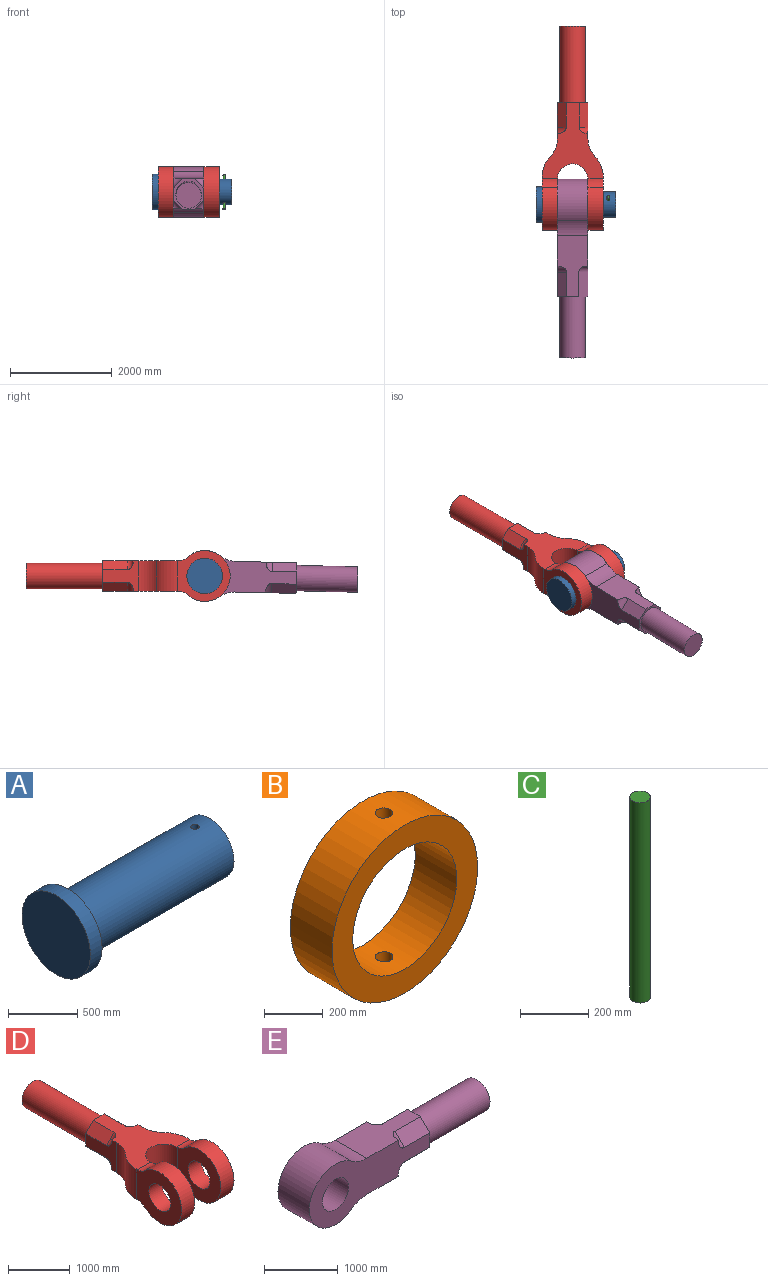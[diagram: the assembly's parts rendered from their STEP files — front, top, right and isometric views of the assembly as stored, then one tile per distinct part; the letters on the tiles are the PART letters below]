
ASSEMBLY  parts=5 mates=5
PART A: 6 faces, bbox 1570x700x700 mm
  f0: cylinder r=250mm len=1450mm, axis (-1,0,0), area 2272006.1mm2, adj f1,f2,f5
  f1: plane 500x500mm, normal (1,0,0), area 196349.5mm2, adj f0
  f2: plane 700x700mm, normal (1,0,0), area 188495.6mm2, adj f0,f3
  f3: cylinder r=350mm len=700mm, axis (-1,0,0), area 263893.8mm2, adj f2,f4
  f4: plane 700x700mm, normal (-1,0,0), area 384845.1mm2, adj f3
  f5: cylinder r=30mm len=500mm, axis (0,0,-1), area 93907.4mm2, adj f0
PART B: 6 faces, bbox 700x200x700 mm
  f0: cylinder r=250mm len=500mm, axis (0,1,0), area 308511.8mm2, adj f2,f3,f4,f5
  f1: cylinder r=350mm len=700mm, axis (0,1,0), area 434178.1mm2, adj f2,f3,f4,f5
  f2: plane 700x700mm, normal (0,-1,0), area 188495.6mm2, adj f0,f1
  f3: plane 700x700mm, normal (0,1,0), area 188495.6mm2, adj f0,f1
  f4: cylinder r=30mm len=101.81mm, axis (0,0,1), area 18898.3mm2, adj f0,f1
  f5: cylinder r=30mm len=101.81mm, axis (0,0,1), area 18898.2mm2, adj f0,f1
PART C: 3 faces, bbox 60x60x720 mm
  f0: cylinder r=30mm len=720mm, axis (0,0,-1), area 135716.8mm2, adj f1,f2
  f1: plane 60x60mm, normal (0,0,1), area 2827.4mm2, adj f0
  f2: plane 60x60mm, normal (0,0,-1), area 2827.4mm2, adj f0
PART D: 36 faces, bbox 1200x4007x1000 mm
  f0: plane 600x600mm, normal (0,1,0), area 103098.5mm2, adj f1,f2,f9,f18,f22,f24,f26,f28
  f1: plane 705.02x600mm, normal (-1,0,0), area 222950.5mm2, adj f0,f2,f7,f18,f24,f25,f26,f27
  f2: plane 1490.1x1200mm, normal (0,0,1), area 810833.6mm2, adj f0,f1,f3,f6,f7,f8,f9,f10
  f3: plane 1040x1000mm, normal (-1,0,0), area 635026.5mm2, adj f2,f6,f13,f15,f17,f18,f21
  f4: plane 1000x1000mm, normal (-1,0,0), area 611025.2mm2, adj f12,f14,f16,f19,f20
  f5: plane 1000x1000mm, normal (1,0,0), area 611025.2mm2, adj f12,f13,f15,f17,f21
  f6: cylinder r=600mm len=600mm, axis (0,0,1), area 272324.3mm2, adj f2,f3,f7,f18
  f7: cylinder r=500mm len=600mm, axis (0,0,1), area 226936.9mm2, adj f1,f2,f6,f18
  f8: cylinder r=600mm len=600mm, axis (0,0,1), area 272324.3mm2, adj f2,f10,f11,f18
  f9: plane 705.02x600mm, normal (1,0,0), area 222950.5mm2, adj f0,f2,f10,f18,f22,f23,f28,f29
  f10: cylinder r=500mm len=600mm, axis (0,0,1), area 226936.9mm2, adj f2,f8,f9,f18
  f11: plane 1040x1000mm, normal (1,0,0), area 635026.5mm2, adj f2,f8,f14,f16,f18,f19,f20
  f12: cylinder r=300mm len=600.39mm, axis (0,0,1), area 565489.3mm2, adj f2,f4,f5,f15,f16,f17,f18,f19
  f13: cylinder r=500mm len=1000mm, axis (1,0,0), area 695514.2mm2, adj f3,f5,f15,f17
  f14: cylinder r=500mm len=1000mm, axis (1,0,0), area 695514.2mm2, adj f4,f11,f16,f19
  f15: cylinder r=250mm len=300.16mm, axis (1,0,0), area 56069.4mm2, adj f2,f3,f5,f12,f13
  f16: cylinder r=250mm len=300.16mm, axis (1,0,0), area 56069.4mm2, adj f2,f4,f11,f12,f14
  f17: cylinder r=250mm len=300.16mm, axis (1,0,0), area 56069.4mm2, adj f3,f5,f12,f13,f18
  f18: plane 1490.1x1200mm, normal (0,0,-1), area 810833.6mm2, adj f0,f1,f3,f6,f7,f8,f9,f10
  f19: cylinder r=250mm len=300.16mm, axis (1,0,0), area 56069.4mm2, adj f4,f11,f12,f14,f18
  f20: cylinder r=250mm len=500mm, axis (1,0,0), area 471238.9mm2, adj f4,f11
  f21: cylinder r=250mm len=500mm, axis (1,0,0), area 471238.9mm2, adj f3,f5
  f22: plane 480x174mm, normal (0.71,0,-0.71), area 118115.1mm2, adj f0,f9,f18,f33
  f23: plane 4.29x4.29mm, normal (0,1,0), area 9.2mm2, adj f9,f18,f33
  f24: plane 480x174mm, normal (-0.71,0,-0.71), area 118115.1mm2, adj f0,f1,f18,f32
  f25: plane 4.29x4.29mm, normal (0,1,0), area 9.2mm2, adj f1,f18,f32
  f26: plane 480x174mm, normal (-0.71,0,0.71), area 118115.1mm2, adj f0,f1,f2,f35
  f27: plane 4.29x4.29mm, normal (0,1,0), area 9.2mm2, adj f1,f2,f35
  f28: plane 480x174mm, normal (0.71,0,0.71), area 118115.1mm2, adj f0,f2,f9,f34
  f29: plane 4.29x4.29mm, normal (0,1,0), area 9.2mm2, adj f2,f9,f34
  f30: cylinder r=250mm len=1507mm, axis (0,-1,0), area 2367190.1mm2, adj f0,f31
  f31: plane 500x500mm, normal (0,1,0), area 196349.5mm2, adj f30
  f32: cylinder r=120mm len=258.85mm, axis (0.71,0,-0.71), area 29944.8mm2, adj f1,f18,f24,f25
  f33: cylinder r=120mm len=258.85mm, axis (0.71,0,0.71), area 29944.8mm2, adj f9,f18,f22,f23
  f34: cylinder r=120mm len=258.85mm, axis (-0.71,0,0.71), area 29944.8mm2, adj f2,f9,f28,f29
  f35: cylinder r=120mm len=258.85mm, axis (-0.71,0,-0.71), area 29944.8mm2, adj f1,f2,f26,f27
PART E: 23 faces, bbox 3505x769.7x1000 mm
  f0: plane 1200x600mm, normal (0,0,1), area 512020.6mm2, adj f2,f3,f6,f8,f9,f10,f13,f14
  f1: plane 1200x600mm, normal (0,0,-1), area 512020.6mm2, adj f2,f5,f6,f8,f11,f12,f15,f16
  f2: plane 2300x1000mm, normal (0,-1,0), area 1188370.1mm2, adj f0,f1,f3,f4,f5,f6,f7,f13
  f3: cylinder r=500mm len=600mm, axis (0,1,0), area 193050.3mm2, adj f0,f2,f4,f8
  f4: cylinder r=500mm len=1000mm, axis (0,1,0), area 1328578.5mm2, adj f2,f3,f5,f8
  f5: cylinder r=500mm len=600mm, axis (0,1,0), area 193050.3mm2, adj f1,f2,f4,f8
  f6: plane 600x600mm, normal (1,0,0), area 98417.7mm2, adj f0,f1,f2,f8,f9,f11,f13,f15
  f7: cylinder r=250mm len=600mm, axis (0,1,0), area 942477.8mm2, adj f2,f8
  f8: plane 2300x1000mm, normal (0,1,0), area 1188370.1mm2, adj f0,f1,f3,f4,f5,f6,f7,f9
  f9: plane 480x180.6mm, normal (0,0.71,0.71), area 122595.3mm2, adj f0,f6,f8,f21
  f10: plane 10.89x10.89mm, normal (1,0,0), area 59.3mm2, adj f0,f8,f21
  f11: plane 480x180.6mm, normal (0,0.71,-0.71), area 122595.3mm2, adj f1,f6,f8,f20
  f12: plane 10.89x10.89mm, normal (1,0,0), area 59.3mm2, adj f1,f8,f20
  f13: plane 480x180.6mm, normal (0,-0.71,0.71), area 122595.3mm2, adj f0,f2,f6,f22
  f14: plane 10.89x10.89mm, normal (1,0,0), area 59.3mm2, adj f0,f2,f22
  f15: plane 480x180.6mm, normal (0,-0.71,-0.71), area 122595.3mm2, adj f1,f2,f6,f19
  f16: plane 10.89x10.89mm, normal (1,0,0), area 59.3mm2, adj f1,f2,f19
  f17: cylinder r=250mm len=1205mm, axis (-1,0,0), area 1892809.6mm2, adj f6,f18
  f18: plane 500x500mm, normal (1,0,0), area 196349.5mm2, adj f17
  f19: cylinder r=120mm len=265.45mm, axis (0,-0.71,0.71), area 31704.1mm2, adj f1,f2,f15,f16
  f20: cylinder r=120mm len=265.45mm, axis (0,-0.71,-0.71), area 31704.1mm2, adj f1,f8,f11,f12
  f21: cylinder r=120mm len=265.45mm, axis (0,0.71,-0.71), area 31704.1mm2, adj f0,f8,f9,f10
  f22: cylinder r=120mm len=265.45mm, axis (0,0.71,0.71), area 31704.1mm2, adj f0,f2,f13,f14
PLACE A rot(axis=(-1,0,0),24.8deg) t=(428.85,-792.19,1431.54)mm
PLACE B rot(axis=(0.7,-0.7,0.15),162.6deg) t=(-396.15,-792.19,1431.54)mm
PLACE C rot(axis=(-1,0,0),24.8deg) t=(278.85,-944.57,1101.01)mm
PLACE D t=(178.85,-1292.19,931.54)mm fixed
PLACE E rot(axis=(0.01,0.01,-1),90deg) t=(-121.15,-792.19,1431.54)mm
MATE revolute E.f7 <-> D.f13  axis (1,0,0) through (-121.15,-792.19,1431.54)mm
MATE slider A.f5 <-> C.f0  axis (0,-0.42,-0.91) through (278.85,-686.25,1661.32)mm
MATE cylindrical B.f1 <-> A.f0  axis (1,0,0) through (-196.15,-792.19,1431.54)mm
MATE planar D.f13 <-> A.f0  axis (-1,0,0) through (-1021.15,-792.19,1431.54)mm
MATE cylindrical A.f0 <-> D.f13  axis (-1,0,0) through (428.85,-792.19,1431.54)mm
